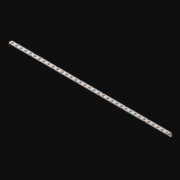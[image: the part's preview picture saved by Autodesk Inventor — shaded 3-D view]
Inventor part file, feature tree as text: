
AUTODESK INVENTOR PART (.ipt)
format: ipt  version: 2021 (Build 250183000, 183)  size: 860,160 bytes
history: native  units: in
note: dims shown in document units (in); Inventor stores cm internally (conversion verified against a paired STEP export)
features: other x70, extrude x70, sketch x2, pattern_linear x1, sheet_metal_op x1
ambient origin geometry x8: Origin, YZ Plane, XZ Plane, XY Plane, X Axis, Y Axis, Z Axis, Center Point
bodies: Solid1 (feature_tree)
feature tree (144):
  pattern_linear  "Rectangular Pattern1"  Spacing1=0.182in  [1 undecoded]
  sketch  "Sketch1"  dims[d0=0.182in]
  other  "Srf1"
  sketch  "Sketch2"  dims[d1=0.063in d2=0.0in d3=0.182in d4=0.063in d5=0.0in d8=0.5in]
  other  "Srf2"
  other  "Srf3"
  other  "Srf5"
  other  "Srf7"
  other  "Srf9"
  other  "Srf11"
  other  "Srf13"
  other  "Srf15"
  other  "Srf17"
  other  "Srf19"
  other  "Srf21"
  other  "Srf23"
  other  "Srf25"
  other  "Srf27"
  other  "Srf29"
  other  "Srf31"
  other  "Srf33"
  other  "Srf35"
  other  "Srf37"
  other  "Srf39"
  other  "Srf41"
  other  "Srf43"
  other  "Srf45"
  other  "Srf47"
  other  "Srf49"
  other  "Srf51"
  other  "Srf53"
  other  "Srf55"
  other  "Srf57"
  other  "Srf59"
  other  "Srf61"
  other  "Srf63"
  other  "Srf65"
  other  "Srf67"
  other  "Srf69"
  other  "Srf4"
  other  "Srf6"
  other  "Srf8"
  other  "Srf10"
  other  "Srf12"
  other  "Srf14"
  other  "Srf16"
  other  "Srf18"
  other  "Srf20"
  other  "Srf22"
  other  "Srf24"
  other  "Srf26"
  other  "Srf28"
  other  "Srf30"
  other  "Srf32"
  other  "Srf34"
  other  "Srf36"
  other  "Srf38"
  other  "Srf40"
  other  "Srf42"
  other  "Srf44"
  other  "Srf46"
  other  "Srf48"
  other  "Srf50"
  other  "Srf52"
  other  "Srf54"
  other  "Srf56"
  other  "Srf58"
  other  "Srf60"
  other  "Srf62"
  other  "Srf64"
  other  "Srf66"
  other  "Srf68"
  other  "Srf70"
  sheet_metal_op  "Fold1"
  extrude  "ExtrusionSrf1"  Depth=0.5in TaperAngle=0.0deg
  extrude  "ExtrusionSrf2"  Depth=0.5in
  extrude  "ExtrusionSrf3"  [1 undecoded]
  extrude  "ExtrusionSrf4"  [1 undecoded]
  extrude  "ExtrusionSrf5"  [1 undecoded]
  extrude  "ExtrusionSrf6"  [1 undecoded]
  extrude  "ExtrusionSrf7"  [1 undecoded]
  extrude  "ExtrusionSrf8"  [1 undecoded]
  extrude  "ExtrusionSrf9"  [1 undecoded]
  extrude  "ExtrusionSrf10"  [1 undecoded]
  extrude  "ExtrusionSrf11"  [1 undecoded]
  extrude  "ExtrusionSrf12"  [1 undecoded]
  extrude  "ExtrusionSrf13"  [1 undecoded]
  extrude  "ExtrusionSrf14"  [1 undecoded]
  extrude  "ExtrusionSrf15"  [1 undecoded]
  extrude  "ExtrusionSrf16"  [1 undecoded]
  extrude  "ExtrusionSrf17"  [1 undecoded]
  extrude  "ExtrusionSrf18"  [1 undecoded]
  extrude  "ExtrusionSrf19"  [1 undecoded]
  extrude  "ExtrusionSrf20"  [1 undecoded]
  extrude  "ExtrusionSrf21"  [1 undecoded]
  extrude  "ExtrusionSrf22"  [1 undecoded]
  extrude  "ExtrusionSrf23"  [1 undecoded]
  extrude  "ExtrusionSrf24"  [1 undecoded]
  extrude  "ExtrusionSrf25"  [1 undecoded]
  extrude  "ExtrusionSrf26"  [1 undecoded]
  extrude  "ExtrusionSrf27"  [1 undecoded]
  extrude  "ExtrusionSrf28"  [1 undecoded]
  extrude  "ExtrusionSrf29"  [1 undecoded]
  extrude  "ExtrusionSrf30"  [1 undecoded]
  extrude  "ExtrusionSrf31"  [1 undecoded]
  extrude  "ExtrusionSrf32"  [1 undecoded]
  extrude  "ExtrusionSrf33"  [1 undecoded]
  extrude  "ExtrusionSrf34"  [1 undecoded]
  extrude  "ExtrusionSrf35"  [1 undecoded]
  extrude  "ExtrusionSrf36"  [1 undecoded]
  extrude  "ExtrusionSrf37"  [1 undecoded]
  extrude  "ExtrusionSrf38"  [1 undecoded]
  extrude  "ExtrusionSrf39"  [1 undecoded]
  extrude  "ExtrusionSrf40"  [1 undecoded]
  extrude  "ExtrusionSrf41"  [1 undecoded]
  extrude  "ExtrusionSrf42"  [1 undecoded]
  extrude  "ExtrusionSrf43"  [1 undecoded]
  extrude  "ExtrusionSrf44"  [1 undecoded]
  extrude  "ExtrusionSrf45"  [1 undecoded]
  extrude  "ExtrusionSrf46"  [1 undecoded]
  extrude  "ExtrusionSrf47"  [1 undecoded]
  extrude  "ExtrusionSrf48"  [1 undecoded]
  extrude  "ExtrusionSrf49"  [1 undecoded]
  extrude  "ExtrusionSrf50"  [1 undecoded]
  extrude  "ExtrusionSrf51"  [1 undecoded]
  extrude  "ExtrusionSrf52"  [1 undecoded]
  extrude  "ExtrusionSrf53"  [1 undecoded]
  extrude  "ExtrusionSrf54"  [1 undecoded]
  extrude  "ExtrusionSrf55"  [1 undecoded]
  extrude  "ExtrusionSrf56"  [1 undecoded]
  extrude  "ExtrusionSrf57"  [1 undecoded]
  extrude  "ExtrusionSrf58"  [1 undecoded]
  extrude  "ExtrusionSrf59"  [1 undecoded]
  extrude  "ExtrusionSrf60"  [1 undecoded]
  extrude  "ExtrusionSrf61"  [1 undecoded]
  extrude  "ExtrusionSrf62"  [1 undecoded]
  extrude  "ExtrusionSrf63"  [1 undecoded]
  extrude  "ExtrusionSrf64"  [1 undecoded]
  extrude  "ExtrusionSrf65"  [1 undecoded]
  extrude  "ExtrusionSrf66"  [1 undecoded]
  extrude  "ExtrusionSrf67"  [1 undecoded]
  extrude  "ExtrusionSrf68"  [1 undecoded]
  extrude  "ExtrusionSrf69"  [1 undecoded]
  extrude  "ExtrusionSrf70"  [1 undecoded]
note: 69 required parameter values undecoded (feature->parameter linkage not recoverable at this tier; creation-order binding heuristic only, values carry confidence <= 0.55)
